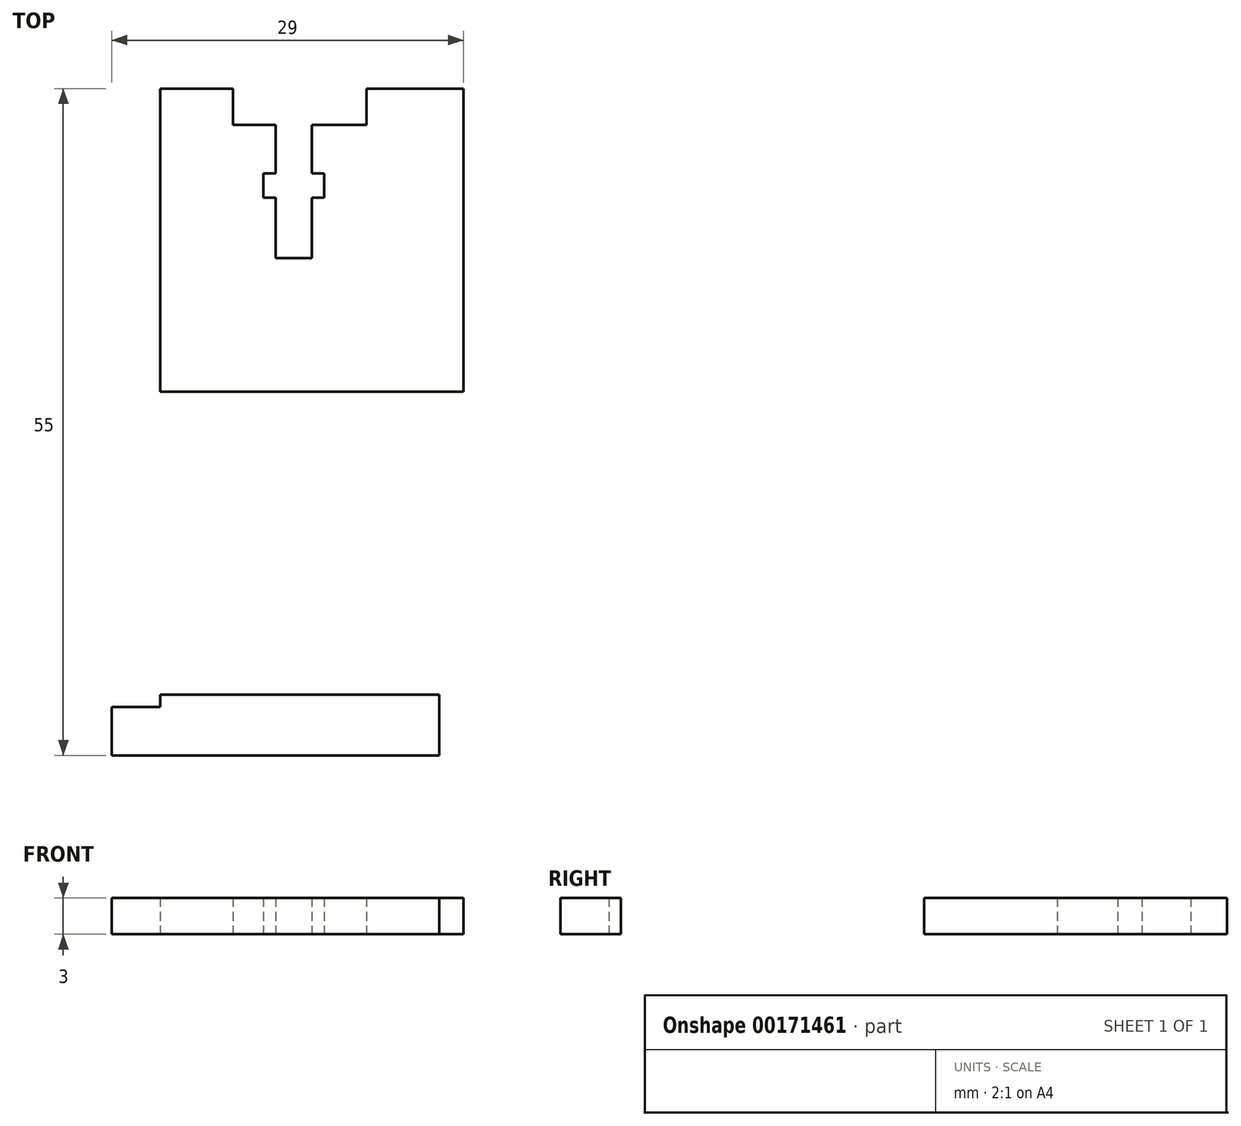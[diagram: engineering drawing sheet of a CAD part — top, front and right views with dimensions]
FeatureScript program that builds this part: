
annotation { "Feature Type Name" : "Feature", "Feature Type Description" : "" }
export const myFeature = defineFeature(function(context is Context, id is Id, definition is map)
    precondition{}
    {
        {
            var Q0;
            Q0=qCreatedBy(makeId("Top.planeOp"),FACE);
            var sketch = newSketch(context, id + "F0", { "sketchPlane" : qUnion([Q0])});
            skLineSegment(sketch, "E0.bottom", {"start": v(12.5, 12.5) * mm, "end": v(-12.5, 12.5) * mm});
            skLineSegment(sketch, "E0.top", {"start": v(-12.5, -12.5) * mm, "end": v(12.5, -12.5) * mm});
            skLineSegment(sketch, "E0.left", {"start": v(-12.5, 12.5) * mm, "end": v(-12.5, -12.5) * mm});
            skLineSegment(sketch, "E0.right", {"start": v(12.5, -12.5) * mm, "end": v(12.5, 12.5) * mm});
            skPoint(sketch, "E0.middle", {"position": v(0, 0) * mm});
            skLineSegment(sketch, "E1.bottom", {"start": v(-12.5, -12.5) * mm, "end": v(-2.5, -12.5) * mm});
            skLineSegment(sketch, "E1.top", {"start": v(-12.5, -37.5) * mm, "end": v(-2.5, -37.5) * mm});
            skLineSegment(sketch, "E1.left", {"start": v(-12.5, -12.5) * mm, "end": v(-12.5, -37.5) * mm});
            skLineSegment(sketch, "E1.right", {"start": v(-2.5, -12.5) * mm, "end": v(-2.5, -37.5) * mm});
            skLineSegment(sketch, "E2.bottom", {"start": v(-12.5, -37.5) * mm, "end": v(10.5, -37.5) * mm});
            skLineSegment(sketch, "E2.top", {"start": v(-12.5, -42.5) * mm, "end": v(10.5, -42.5) * mm});
            skLineSegment(sketch, "E2.left", {"start": v(-12.5, -37.5) * mm, "end": v(-12.5, -42.5) * mm});
            skLineSegment(sketch, "E2.right", {"start": v(10.5, -37.5) * mm, "end": v(10.5, -42.5) * mm});
            skLineSegment(sketch, "E3.bottom", {"start": v(-12.5, -42.5) * mm, "end": v(-16.5, -42.5) * mm});
            skLineSegment(sketch, "E3.top", {"start": v(-12.5, -38.5) * mm, "end": v(-16.5, -38.5) * mm});
            skLineSegment(sketch, "E3.left", {"start": v(-12.5, -42.5) * mm, "end": v(-12.5, -38.5) * mm});
            skLineSegment(sketch, "E3.right", {"start": v(-16.5, -42.5) * mm, "end": v(-16.5, -38.5) * mm});
            skLineSegment(sketch, "E4.bottom", {"start": v(10.5, -42.5) * mm, "end": v(4.5, -42.5) * mm});
            skLineSegment(sketch, "E4.top", {"start": v(10.5, -76.5) * mm, "end": v(4.5, -76.5) * mm});
            skLineSegment(sketch, "E4.left", {"start": v(10.5, -42.5) * mm, "end": v(10.5, -76.5) * mm});
            skLineSegment(sketch, "E4.right", {"start": v(4.5, -42.5) * mm, "end": v(4.5, -76.5) * mm});
            skLineSegment(sketch, "E5.bottom", {"start": v(-6.5, 12.5) * mm, "end": v(4.5, 12.5) * mm});
            skLineSegment(sketch, "E5.top", {"start": v(-6.5, 9.5) * mm, "end": v(4.5, 9.5) * mm});
            skLineSegment(sketch, "E5.left", {"start": v(-6.5, 12.5) * mm, "end": v(-6.5, 9.5) * mm});
            skLineSegment(sketch, "E5.right", {"start": v(4.5, 12.5) * mm, "end": v(4.5, 9.5) * mm});
            skLineSegment(sketch, "E6.bottom", {"start": v(-3, 9.5) * mm, "end": v(0, 9.5) * mm});
            skLineSegment(sketch, "E6.top", {"start": v(-3, 5.5) * mm, "end": v(0, 5.5) * mm});
            skLineSegment(sketch, "E6.left", {"start": v(-3, 9.5) * mm, "end": v(-3, 5.5) * mm});
            skLineSegment(sketch, "E6.right", {"start": v(0, 9.5) * mm, "end": v(0, 5.5) * mm});
            skLineSegment(sketch, "E7", {"start": v(-3, 5.5) * mm, "end": v(-4, 5.5) * mm});
            skLineSegment(sketch, "E8", {"start": v(0, 5.5) * mm, "end": v(1, 5.5) * mm});
            skLineSegment(sketch, "E9.bottom", {"start": v(-4, 5.5) * mm, "end": v(1, 5.5) * mm});
            skLineSegment(sketch, "E9.top", {"start": v(-4, 3.5) * mm, "end": v(1, 3.5) * mm});
            skLineSegment(sketch, "E9.left", {"start": v(-4, 5.5) * mm, "end": v(-4, 3.5) * mm});
            skLineSegment(sketch, "E9.right", {"start": v(1, 5.5) * mm, "end": v(1, 3.5) * mm});
            skLineSegment(sketch, "E10.bottom", {"start": v(-3, 3.5) * mm, "end": v(0, 3.5) * mm});
            skLineSegment(sketch, "E10.top", {"start": v(-3, -1.5) * mm, "end": v(0, -1.5) * mm});
            skLineSegment(sketch, "E10.left", {"start": v(-3, 3.5) * mm, "end": v(-3, -1.5) * mm});
            skLineSegment(sketch, "E10.right", {"start": v(0, 3.5) * mm, "end": v(0, -1.5) * mm});
            skSolve(sketch);
        }
        {
            var Q0;
            Q0=makeQuery(id+"F0.imprint","IMPRINT",FACE,{"disambiguationData":[TD([[makeQuery(id+"F0.imprint","IMPRINT",EDGE,{"derivedFrom":sQuery(id+"F0.wireOp",EDGE,"E3.bottom")}),-1.0]])]});
            var Q1;
            Q1=makeQuery(id+"F0.imprint","IMPRINT",FACE,{"disambiguationData":[TD([[makeQuery(id+"F0.imprint","IMPRINT",EDGE,{"derivedFrom":sQuery(id+"F0.wireOp",EDGE,"E4.bottom")}),1.0]])]});
            var Q2;
            Q2=makeQuery(id+"F0.imprint","IMPRINT",FACE,{"disambiguationData":[TD([[makeQuery(id+"F0.imprint","IMPRINT",EDGE,{"derivedFrom":sQuery(id+"F0.wireOp",EDGE,"E1.bottom")}),-1.0]])]});
            var Q3;
            Q3=makeQuery(id+"F0.imprint","IMPRINT",FACE,{"disambiguationData":[TD([[makeQuery(id+"F0.imprint","IMPRINT",EDGE,{"derivedFrom":sQuery(id+"F0.wireOp",EDGE,"E2.top")}),1.0]])]});
            var Q4;
            Q4=makeQuery(id+"F0.imprint","IMPRINT",FACE,{"disambiguationData":[TD([[makeQuery(id+"F0.imprint","IMPRINT",EDGE,{"derivedFrom":sQuery(id+"F0.wireOp",EDGE,"E0.top")}),1.0]])]});
            extrude(context, id + "F1", {"entities" : qUnion([Q0, Q1, Q2, Q3, Q4]), "depth" : 3 * mm});
        }
    });
